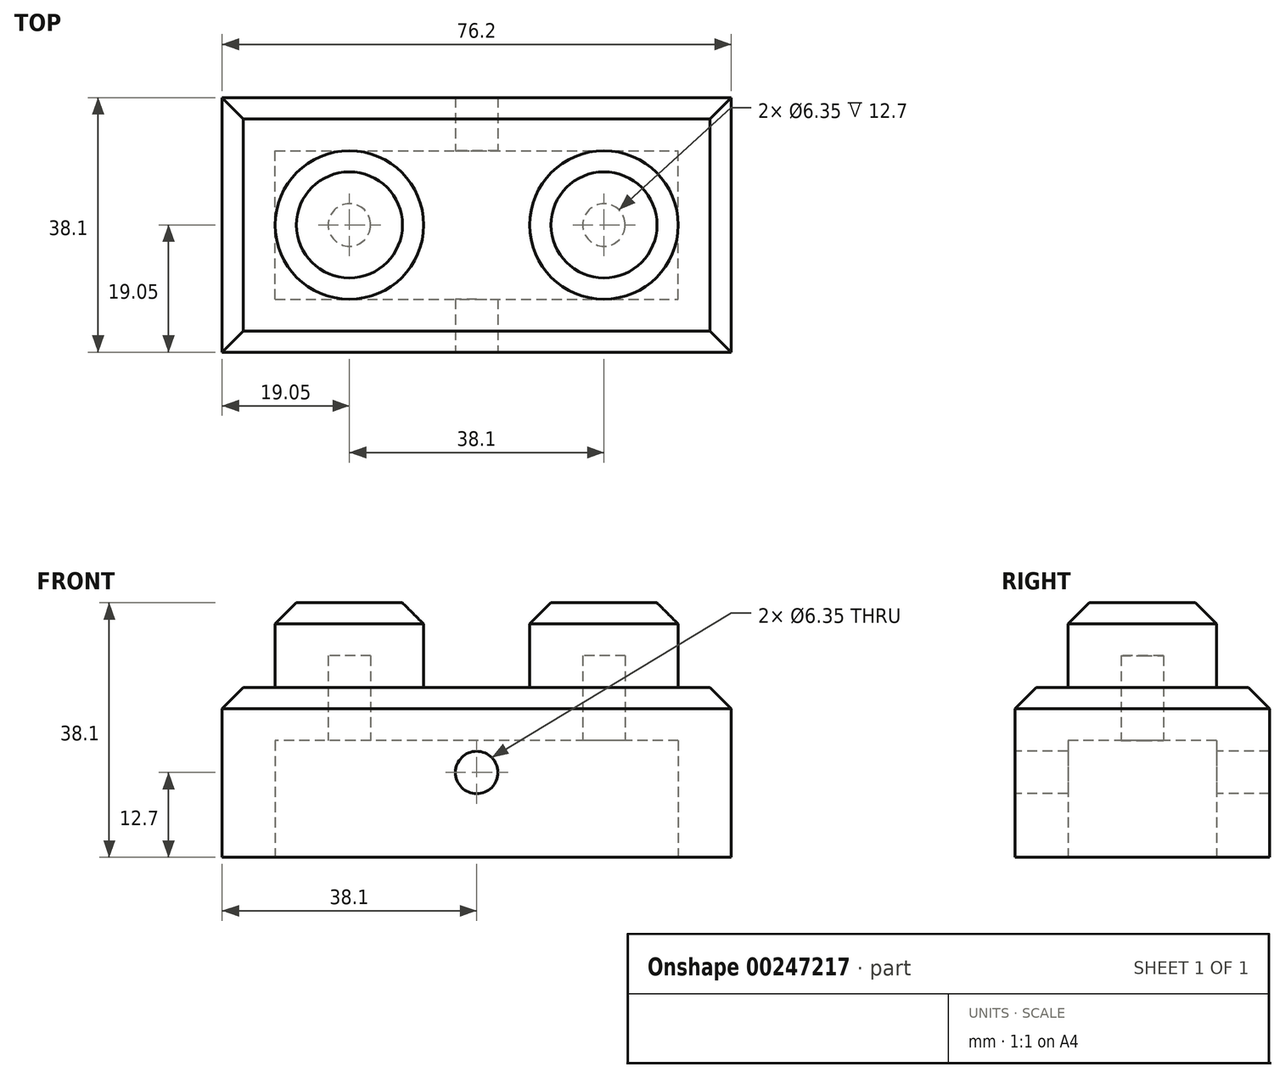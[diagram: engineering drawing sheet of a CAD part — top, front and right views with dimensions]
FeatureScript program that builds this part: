
annotation { "Feature Type Name" : "Feature", "Feature Type Description" : "" }
export const myFeature = defineFeature(function(context is Context, id is Id, definition is map)
    precondition{}
    {
        {
            var Q0;
            Q0=qCreatedBy(makeId("Top.planeOp"),FACE);
            var sketch = newSketch(context, id + "F0", { "sketchPlane" : qUnion([Q0])});
            skLineSegment(sketch, "E0.bottom", {"start": v(0, 0) * mm, "end": v(76.2, 0) * mm});
            skLineSegment(sketch, "E0.top", {"start": v(0, 38.1) * mm, "end": v(76.2, 38.1) * mm});
            skLineSegment(sketch, "E0.left", {"start": v(0, 0) * mm, "end": v(0, 38.1) * mm});
            skLineSegment(sketch, "E0.right", {"start": v(76.2, 0) * mm, "end": v(76.2, 38.1) * mm});
            skSolve(sketch);
        }
        {
            var Q0;
            Q0 = qSketchRegion(id + "F0", true);
            extrude(context, id + "F1", {"entities" : qUnion([Q0]), "depth" : 25.4 * mm});
        }
        {
            var Q0;
            Q0=makeQuery(id+"F1.opExtrude","CAP_FACE",FACE,{"disambiguationData":[OSD([sQuery(id+"F0.wireOp",EDGE,"E0.bottom"),sQuery(id+"F0.wireOp",EDGE,"E0.top"),sQuery(id+"F0.wireOp",EDGE,"E0.left"),sQuery(id+"F0.wireOp",EDGE,"E0.right")])],"isStart":false});
            var sketch = newSketch(context, id + "F2", { "sketchPlane" : qUnion([Q0])});
            skCircle(sketch, "E1", {"center": v(19.05, 19.05) * mm, "radius": 11.11 * mm});
            skCircle(sketch, "E2", {"center": v(57.15, 19.05) * mm, "radius": 11.11 * mm});
            skSolve(sketch);
        }
        {
            var Q0;
            Q0 = qSketchRegion(id + "F2", true);
            extrude(context, id + "F3", {"entities" : qUnion([Q0]), "operationType" : NewBodyOperationType.ADD, "depth" : 12.7 * mm});
        }
        {
            var Q0;
            Q0=makeQuery(id+"F3.opExtrude","CAP_EDGE",EDGE,{"disambiguationData":[OSD([sQuery(id+"F2.wireOp",EDGE,"E1")])],"isStart":false});
            var Q1;
            Q1=makeQuery(id+"F1.opExtrude","CAP_EDGE",EDGE,{"disambiguationData":[OSD([sQuery(id+"F0.wireOp",EDGE,"E0.left")])],"isStart":false});
            var Q2;
            Q2=makeQuery(id+"F1.opExtrude","CAP_EDGE",EDGE,{"disambiguationData":[OSD([sQuery(id+"F0.wireOp",EDGE,"E0.bottom")])],"isStart":false});
            var Q3;
            Q3=makeQuery(id+"F1.opExtrude","CAP_EDGE",EDGE,{"disambiguationData":[OSD([sQuery(id+"F0.wireOp",EDGE,"E0.right")])],"isStart":false});
            var Q4;
            Q4=makeQuery(id+"F1.opExtrude","CAP_EDGE",EDGE,{"disambiguationData":[OSD([sQuery(id+"F0.wireOp",EDGE,"E0.top")])],"isStart":false});
            var Q5;
            Q5=makeQuery(id+"F3.opExtrude","CAP_EDGE",EDGE,{"disambiguationData":[OSD([sQuery(id+"F2.wireOp",EDGE,"E2")])],"isStart":false});
            chamfer(context, id + "F4", {"entities" : qUnion([Q0, Q1, Q2, Q3, Q4, Q5]), "width" : 3.17 * mm, "tangentPropagation" : true});
        }
        {
            var Q0;
            Q0=makeQuery(id+"F1.opExtrude","CAP_FACE",FACE,{"disambiguationData":[OSD([sQuery(id+"F0.wireOp",EDGE,"E0.bottom"),sQuery(id+"F0.wireOp",EDGE,"E0.top"),sQuery(id+"F0.wireOp",EDGE,"E0.left"),sQuery(id+"F0.wireOp",EDGE,"E0.right")])],"isStart":true});
            shell(context, id + "F5", {"entities" : qUnion([Q0]), "thickness" : 7.94 * mm});
        }
        {
            var Q0;
            Q0=makeQuery(id+"F1.opExtrude","SWEPT_FACE",FACE,{"disambiguationData":[OSD([sQuery(id+"F0.wireOp",EDGE,"E0.bottom")])]});
            var sketch = newSketch(context, id + "F6", { "sketchPlane" : qUnion([Q0])});
            skCircle(sketch, "E3", {"center": v(38.1, 12.7) * mm, "radius": 3.18 * mm});
            skSolve(sketch);
        }
        {
            var Q0;
            Q0 = qSketchRegion(id + "F6", true);
            extrude(context, id + "F7", {"entities" : qUnion([Q0]), "operationType" : NewBodyOperationType.REMOVE, "oppositeDirection" : true, "depth" : 50.8 * mm});
        }
    });
